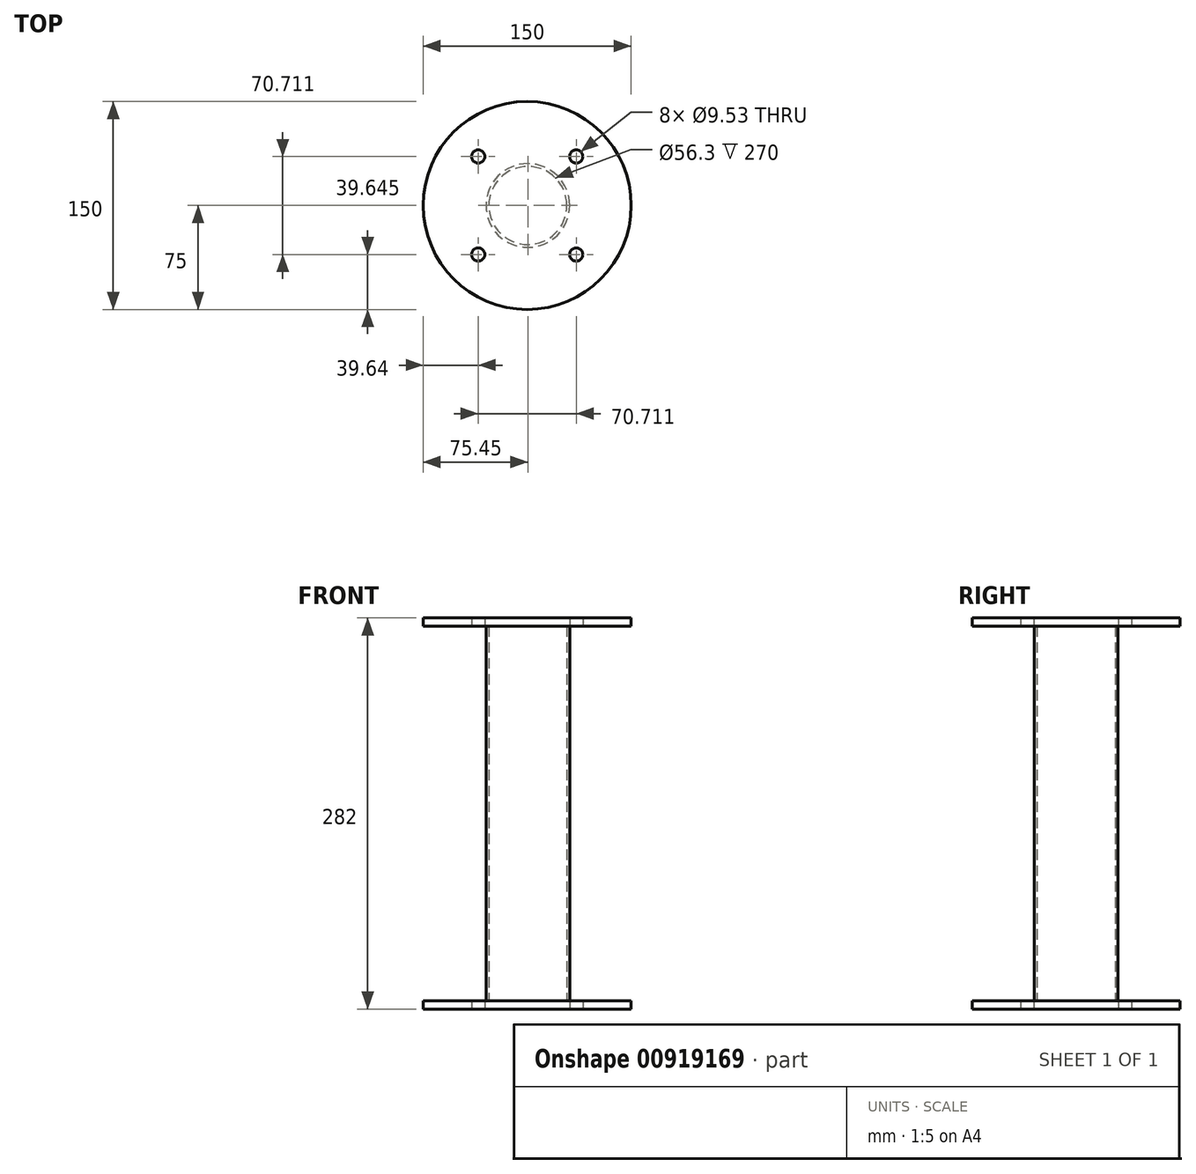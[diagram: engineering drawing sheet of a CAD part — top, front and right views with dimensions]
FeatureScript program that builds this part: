
annotation { "Feature Type Name" : "Feature", "Feature Type Description" : "" }
export const myFeature = defineFeature(function(context is Context, id is Id, definition is map)
    precondition{}
    {
        {
            var Q0;
            Q0=qCreatedBy(makeId("Top.planeOp"),FACE);
            var sketch = newSketch(context, id + "F0", { "sketchPlane" : qUnion([Q0])});
            skLineSegment(sketch, "E0", {"start": v(-0.45, 0) * mm, "end": v(49.55, 0) * mm, "construction": true});
            skCircle(sketch, "E1", {"center": v(34.9, 35.36) * mm, "radius": 4.76 * mm});
            skLineSegment(sketch, "E2.1.0", {"start": v(-0.45, 0) * mm, "end": v(-0.45, 40) * mm, "construction": true});
            skCircle(sketch, "E2.1.1", {"center": v(-35.8, 35.36) * mm, "radius": 4.76 * mm});
            skLineSegment(sketch, "E2.2.0", {"start": v(-0.45, 0) * mm, "end": v(-40.45, 0) * mm, "construction": true});
            skCircle(sketch, "E2.2.1", {"center": v(-35.8, -35.36) * mm, "radius": 4.76 * mm});
            skLineSegment(sketch, "E2.3.0", {"start": v(-0.45, 0) * mm, "end": v(-0.45, -40) * mm, "construction": true});
            skCircle(sketch, "E2.3.1", {"center": v(34.9, -35.36) * mm, "radius": 4.76 * mm});
            skPoint(sketch, "E2.center", {"position": v(-0.45, 0) * mm});
            skCircle(sketch, "E3", {"center": v(-0.45, 0) * mm, "radius": 75 * mm});
            skSolve(sketch);
        }
        {
            var Q0;
            Q0=makeQuery(id+"F0.imprint","IMPRINT",FACE,{"disambiguationData":[TD([[makeQuery(id+"F0.imprint","IMPRINT",EDGE,{"derivedFrom":sQuery(id+"F0.wireOp",EDGE,"E1")}),-1.0]])]});
            extrude(context, id + "F1", {"entities" : qUnion([Q0]), "depth" : 6 * mm, "offsetDistance" : 25 * mm});
        }
        {
            var Q0;
            Q0=makeQuery(id+"F1.opExtrude","CAP_FACE",FACE,{"disambiguationData":[OSD([sQuery(id+"F0.wireOp",EDGE,"E1"),sQuery(id+"F0.wireOp",EDGE,"E2.1.1"),sQuery(id+"F0.wireOp",EDGE,"E2.2.1"),sQuery(id+"F0.wireOp",EDGE,"E2.3.1"),sQuery(id+"F0.wireOp",EDGE,"E3")])],"isStart":false});
            var sketch = newSketch(context, id + "F2", { "sketchPlane" : qUnion([Q0])});
            skCircle(sketch, "E4", {"center": v(0, 0) * mm, "radius": 30.15 * mm});
            skCircle(sketch, "E5.0", {"center": v(0, 0) * mm, "radius": 28.15 * mm});
            skSolve(sketch);
        }
        {
            var Q0;
            Q0 = qSketchRegion(id + "F2", true);
            extrude(context, id + "F3", {"entities" : qUnion([Q0]), "operationType" : NewBodyOperationType.ADD, "depth" : 270 * mm, "offsetDistance" : 25 * mm});
        }
        {
            var Q0;
            Q0=makeQuery(id+"F3.opExtrude","CAP_FACE",FACE,{"disambiguationData":[OSD([sQuery(id+"F2.wireOp",EDGE,"E4"),sQuery(id+"F2.wireOp",EDGE,"E5.0")])],"isStart":false});
            cPlane(context, id + "F4", {"entities" : qUnion([Q0]), "cplaneType" : CPlaneType.OFFSET, "offset" : 0 * mm, "width" : 150 * mm, "height" : 150 * mm});
        }
        {
            var Q0;
            Q0=qCreatedBy(id+"F4.planeOp",FACE);
            var sketch = newSketch(context, id + "F5", { "sketchPlane" : qUnion([Q0])});
            skLineSegment(sketch, "E6", {"start": v(-0.45, 0) * mm, "end": v(49.55, 0) * mm, "construction": true});
            skCircle(sketch, "E7", {"center": v(34.9, 35.36) * mm, "radius": 4.76 * mm});
            skLineSegment(sketch, "E8.1.0", {"start": v(-0.45, 0) * mm, "end": v(-0.45, 40) * mm, "construction": true});
            skCircle(sketch, "E8.1.1", {"center": v(-35.8, 35.36) * mm, "radius": 4.76 * mm});
            skLineSegment(sketch, "E8.2.0", {"start": v(-0.45, 0) * mm, "end": v(-40.45, 0) * mm, "construction": true});
            skCircle(sketch, "E8.2.1", {"center": v(-35.8, -35.36) * mm, "radius": 4.76 * mm});
            skLineSegment(sketch, "E8.3.0", {"start": v(-0.45, 0) * mm, "end": v(-0.45, -40) * mm, "construction": true});
            skCircle(sketch, "E8.3.1", {"center": v(34.9, -35.36) * mm, "radius": 4.76 * mm});
            skPoint(sketch, "E8.center", {"position": v(-0.45, 0) * mm});
            skCircle(sketch, "E9", {"center": v(-0.45, 0) * mm, "radius": 75 * mm});
            skSolve(sketch);
        }
        {
            var Q0;
            Q0=makeQuery(id+"F5.imprint","IMPRINT",FACE,{"disambiguationData":[TD([[makeQuery(id+"F5.imprint","IMPRINT",EDGE,{"derivedFrom":sQuery(id+"F5.wireOp",EDGE,"E7")}),-1.0]])]});
            extrude(context, id + "F6", {"entities" : qUnion([Q0]), "operationType" : NewBodyOperationType.ADD, "depth" : 6 * mm, "offsetDistance" : 25 * mm});
        }
    });
